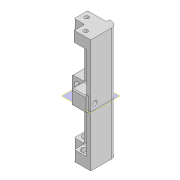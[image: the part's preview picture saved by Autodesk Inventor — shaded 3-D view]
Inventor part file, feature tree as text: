
AUTODESK INVENTOR PART (.ipt)
format: ipt  version: 2020 (Build 240168000, 168)  size: 373,248 bytes
history: native  units: mm
features: extrude x13, sketch x13, other x7, fillet x3
ambient origin geometry x8: Origin, YZ Plane, XZ Plane, XY Plane, X Axis, Y Axis, Z Axis, Center Point
bodies: Body1 (feature_tree)
feature tree (36):
  other  "Sólido1"
  extrude  "Extrusão1"  Depth=16.0mm
  extrude  "Extrusão2"  Depth=3.0mm
  extrude  "Extrusão3"  Depth=3.0mm
  extrude  "Extrusão4"  Depth=6.0mm
  extrude  "Extrusão5"  Depth=8.0mm
  fillet  "Arredondamento1"  Radius=110.0mm
  extrude  "Extrusão6"  Depth=10.0mm
  extrude  "Extrusão7"  TaperAngle=0.0deg  [1 undecoded]
  other  "Plano de trabalho1"
  extrude  "Extrusão9"  Depth=5.0mm
  extrude  "Extrusão10"  Depth=10.0mm
  extrude  "Extrusão11"  Depth=4.0mm
  extrude  "Extrusão12"  Depth=5.0mm
  extrude  "Extrusão13"  Depth=1.0mm TaperAngle=0.0deg
  fillet  "Arredondamento2"  Radius=1.0mm
  extrude  "Extrusão14"  Depth=6.95mm
  fillet  "Arredondamento3"  Radius=6.95mm
  sketch  "Esboço1"  dims[d0=16.0mm d1=16.0mm]
  sketch  "Esboço2"  dims[d2=8.0mm d3=3.0mm]
  sketch  "Esboço3"  dims[d4=8.0mm d5=3.0mm]
  sketch  "Esboço4"  dims[d6=6.0mm d7=5.2mm]
  sketch  "Esboço5"  dims[d8=8.0mm d9=8.0mm d10=110.0mm d11=0.0mm]
  sketch  "Esboço6"  dims[d12=10.0mm d13=10.0mm]
  sketch  "Esboço7"  dims[d14=10.0mm d15=0.0mm d16=0.0mm]
  other  "Contorno projetado1"
  other  "Contorno projetado2"
  sketch  "Esboço9"  dims[d17=4.0mm d18=5.0mm]
  other  "Contorno projetado3"
  other  "Contorno projetado4"
  sketch  "Esboço10"  dims[d19=200.0mm d20=0.0mm d21=10.0mm]
  sketch  "Esboço11"  dims[d22=10.0mm d23=0.0mm d24=4.0mm]
  sketch  "Esboço12"  dims[d25=5.0mm d26=7.0mm]
  sketch  "Esboço13"  dims[d27=6.0mm d28=200.0mm d29=0.0mm d30=1.0mm]
  sketch  "Esboço14"  dims[d31=13.0mm d32=6.95mm d33=6.95mm d34=4.0mm d35=0.0mm d36=4.0mm d37=0.0mm d38=0.0mm d44=0.0mm d45=-50.0mm d46=12.0mm d47=12.0mm d48=2.0mm d49=0.0mm d50=12.0mm d51=0.0mm d52=4.5mm d53=6.0mm d54=20.0mm d55=0.0mm d56=4.5mm d57=6.0mm d58=20.0mm d59=0.0mm d60=6.95mm d61=4.0mm d62=0.0mm d63=6.95mm d64=4.0mm d65=0.0mm d66=1.0mm d67=3.0mm d68=0.0mm d69=1.0mm d70=0.0mm d71=1.0mm]
  other  "Contorno projetado5"
note: 1 required parameter value undecoded (feature->parameter linkage not recoverable at this tier; creation-order binding heuristic only, values carry confidence <= 0.55)
